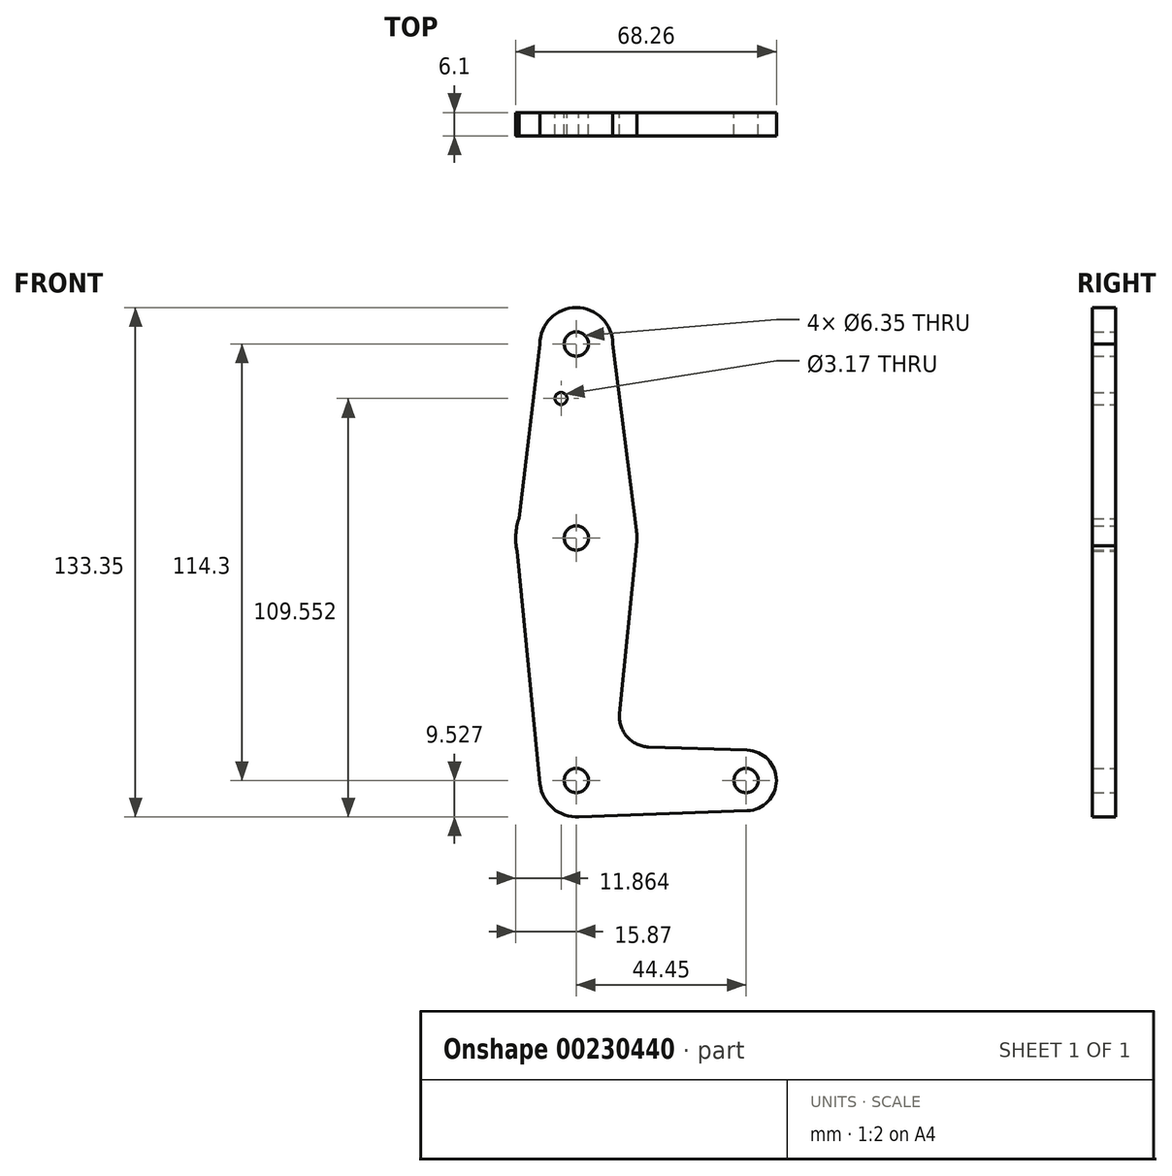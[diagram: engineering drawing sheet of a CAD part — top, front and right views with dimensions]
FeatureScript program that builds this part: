
annotation { "Feature Type Name" : "Feature", "Feature Type Description" : "" }
export const myFeature = defineFeature(function(context is Context, id is Id, definition is map)
    precondition{}
    {
        {
            var Q0;
            Q0=qCreatedBy(makeId("Front.planeOp"),FACE);
            var sketch = newSketch(context, id + "F0", { "sketchPlane" : qUnion([Q0])});
            skLineSegment(sketch, "E0", {"start": v(-44.45, 50.47) * mm, "end": v(-44.45, -63.83) * mm, "construction": true});
            skCircle(sketch, "E1", {"center": v(-44.45, 50.47) * mm, "radius": 9.53 * mm});
            skCircle(sketch, "E2", {"center": v(-44.45, -0.33) * mm, "radius": 15.88 * mm});
            skCircle(sketch, "E3", {"center": v(-44.45, -63.83) * mm, "radius": 9.53 * mm});
            skCircle(sketch, "E4", {"center": v(-44.45, 50.47) * mm, "radius": 3.18 * mm});
            skCircle(sketch, "E5", {"center": v(-48.46, 36.2) * mm, "radius": 1.59 * mm});
            skCircle(sketch, "E6", {"center": v(-44.45, -0.33) * mm, "radius": 3.18 * mm});
            skCircle(sketch, "E7", {"center": v(-44.45, -63.83) * mm, "radius": 3.18 * mm});
            skLineSegment(sketch, "E8", {"start": v(-34.93, 50.47) * mm, "end": v(-28.7, 1.68) * mm});
            skLineSegment(sketch, "E9", {"start": v(-53.98, 50.47) * mm, "end": v(-59.47, 4.8) * mm});
            skLineSegment(sketch, "E10", {"start": v(-60.32, 0) * mm, "end": v(-53.93, -64.77) * mm});
            skLineSegment(sketch, "E11", {"start": v(-44.45, -63.83) * mm, "end": v(0, -63.83) * mm, "construction": true});
            skCircle(sketch, "E12", {"center": v(0, -63.83) * mm, "radius": 7.94 * mm});
            skLineSegment(sketch, "E13", {"start": v(-28.7, -2.34) * mm, "end": v(-33.12, -46.32) * mm});
            skLineSegment(sketch, "E14", {"start": v(-25.47, -55.06) * mm, "end": v(0.26, -55.9) * mm});
            skLineSegment(sketch, "E15", {"start": v(-44.46, -73.36) * mm, "end": v(0.28, -71.77) * mm});
            skArc(sketch, "E16.filletArc", {"start": v(-33.12, -46.32) * mm, "mid": v(-31.2, -52.35) * mm, "end": v(-25.47, -55.06) * mm});
            skCircle(sketch, "E17", {"center": v(0, -63.83) * mm, "radius": 3.18 * mm});
            skSolve(sketch);
        }
        {
            var Q0;
            Q0 = qSketchRegion(id + "F0", true);
            extrude(context, id + "F1", {"entities" : qUnion([Q0]), "depth" : 3.05 * mm});
        }
        {
            var Q0;
            Q0 = qSketchRegion(id + "F0", true);
            var Q1;
            Q1=makeQuery(id+"F1.opExtrude","CAP_FACE",FACE,{"disambiguationData":[OSD([sQuery(id+"F0.wireOp",EDGE,"E1"),sQuery(id+"F0.wireOp",EDGE,"E2"),sQuery(id+"F0.wireOp",EDGE,"E3"),sQuery(id+"F0.wireOp",EDGE,"E4"),sQuery(id+"F0.wireOp",EDGE,"E5"),sQuery(id+"F0.wireOp",EDGE,"E6"),sQuery(id+"F0.wireOp",EDGE,"E7"),sQuery(id+"F0.wireOp",EDGE,"E8"),sQuery(id+"F0.wireOp",EDGE,"E9"),sQuery(id+"F0.wireOp",EDGE,"E10"),sQuery(id+"F0.wireOp",EDGE,"E12"),sQuery(id+"F0.wireOp",EDGE,"E13"),sQuery(id+"F0.wireOp",EDGE,"E14"),sQuery(id+"F0.wireOp",EDGE,"E15"),sQuery(id+"F0.wireOp",EDGE,"E16.filletArc"),sQuery(id+"F0.wireOp",EDGE,"E17")])],"isStart":false});
            extrude(context, id + "F2", {"entities" : qUnion([Q0, Q1]), "operationType" : NewBodyOperationType.ADD, "depth" : 3.05 * mm});
        }
    });
